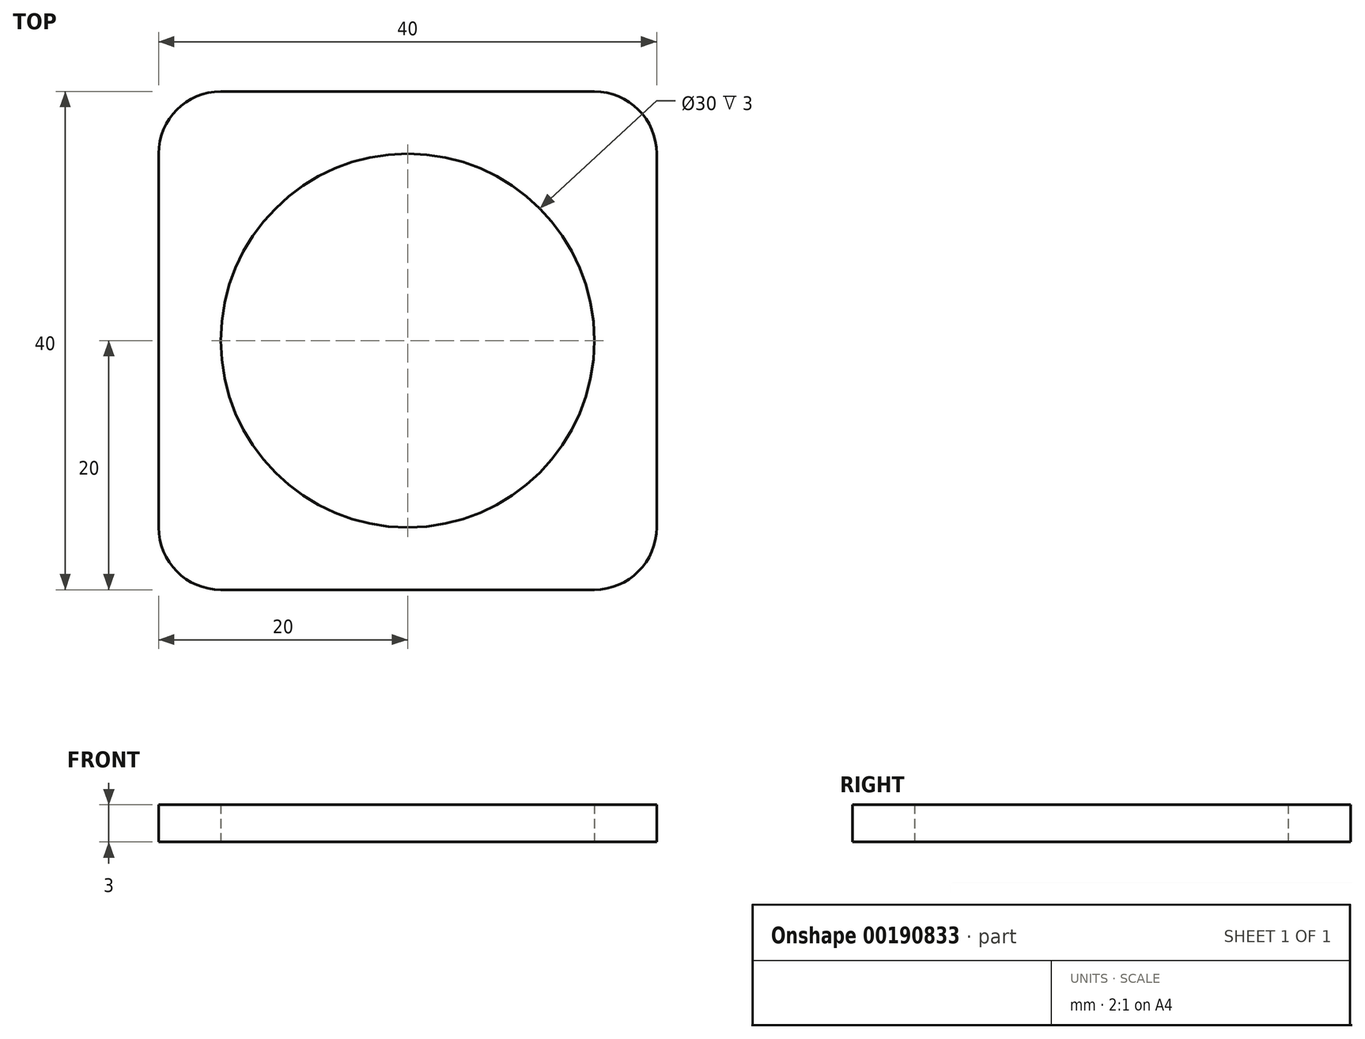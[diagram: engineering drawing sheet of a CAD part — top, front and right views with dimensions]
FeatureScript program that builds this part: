
annotation { "Feature Type Name" : "Feature", "Feature Type Description" : "" }
export const myFeature = defineFeature(function(context is Context, id is Id, definition is map)
    precondition{}
    {
        {
            var Q0;
            Q0=qCreatedBy(makeId("Top.planeOp"),FACE);
            var sketch = newSketch(context, id + "F0", { "sketchPlane" : qUnion([Q0])});
            skLineSegment(sketch, "E0.bottom", {"start": v(-20, 20) * mm, "end": v(20, 20) * mm});
            skLineSegment(sketch, "E0.top", {"start": v(-20, -20) * mm, "end": v(20, -20) * mm});
            skLineSegment(sketch, "E0.left", {"start": v(-20, 20) * mm, "end": v(-20, -20) * mm});
            skLineSegment(sketch, "E0.right", {"start": v(20, 20) * mm, "end": v(20, -20) * mm});
            skPoint(sketch, "E0.middle", {"position": v(0, 0) * mm});
            skCircle(sketch, "E1", {"center": v(0, 0) * mm, "radius": 15 * mm});
            skSolve(sketch);
        }
        {
            var Q0;
            Q0 = qSketchRegion(id + "F0", true);
            extrude(context, id + "F1", {"entities" : qUnion([Q0]), "depth" : 3 * mm, "offsetDistance" : 25 * mm});
        }
        {
            var Q0;
            Q0=makeQuery(id+"F1.opExtrude","SWEPT_EDGE",EDGE,{"disambiguationData":[OSD([sQuery(id+"F0.wireOp",EDGE,"E0.bottom"),sQuery(id+"F0.wireOp",EDGE,"E0.left")])]});
            var Q1;
            Q1=makeQuery(id+"F1.opExtrude","SWEPT_EDGE",EDGE,{"disambiguationData":[OSD([sQuery(id+"F0.wireOp",EDGE,"E0.bottom"),sQuery(id+"F0.wireOp",EDGE,"E0.right")])]});
            var Q2;
            Q2=makeQuery(id+"F1.opExtrude","SWEPT_EDGE",EDGE,{"disambiguationData":[OSD([sQuery(id+"F0.wireOp",EDGE,"E0.top"),sQuery(id+"F0.wireOp",EDGE,"E0.left")])]});
            var Q3;
            Q3=makeQuery(id+"F1.opExtrude","SWEPT_EDGE",EDGE,{"disambiguationData":[OSD([sQuery(id+"F0.wireOp",EDGE,"E0.top"),sQuery(id+"F0.wireOp",EDGE,"E0.right")])]});
            fillet(context, id + "F2", {"entities" : qUnion([Q0, Q1, Q2, Q3]), "tangentPropagation" : true, "radius" : 5 * mm, "defaultsChanged" : false, "vertexSettings" : [], "allowEdgeOverflow" : false});
        }
    });
